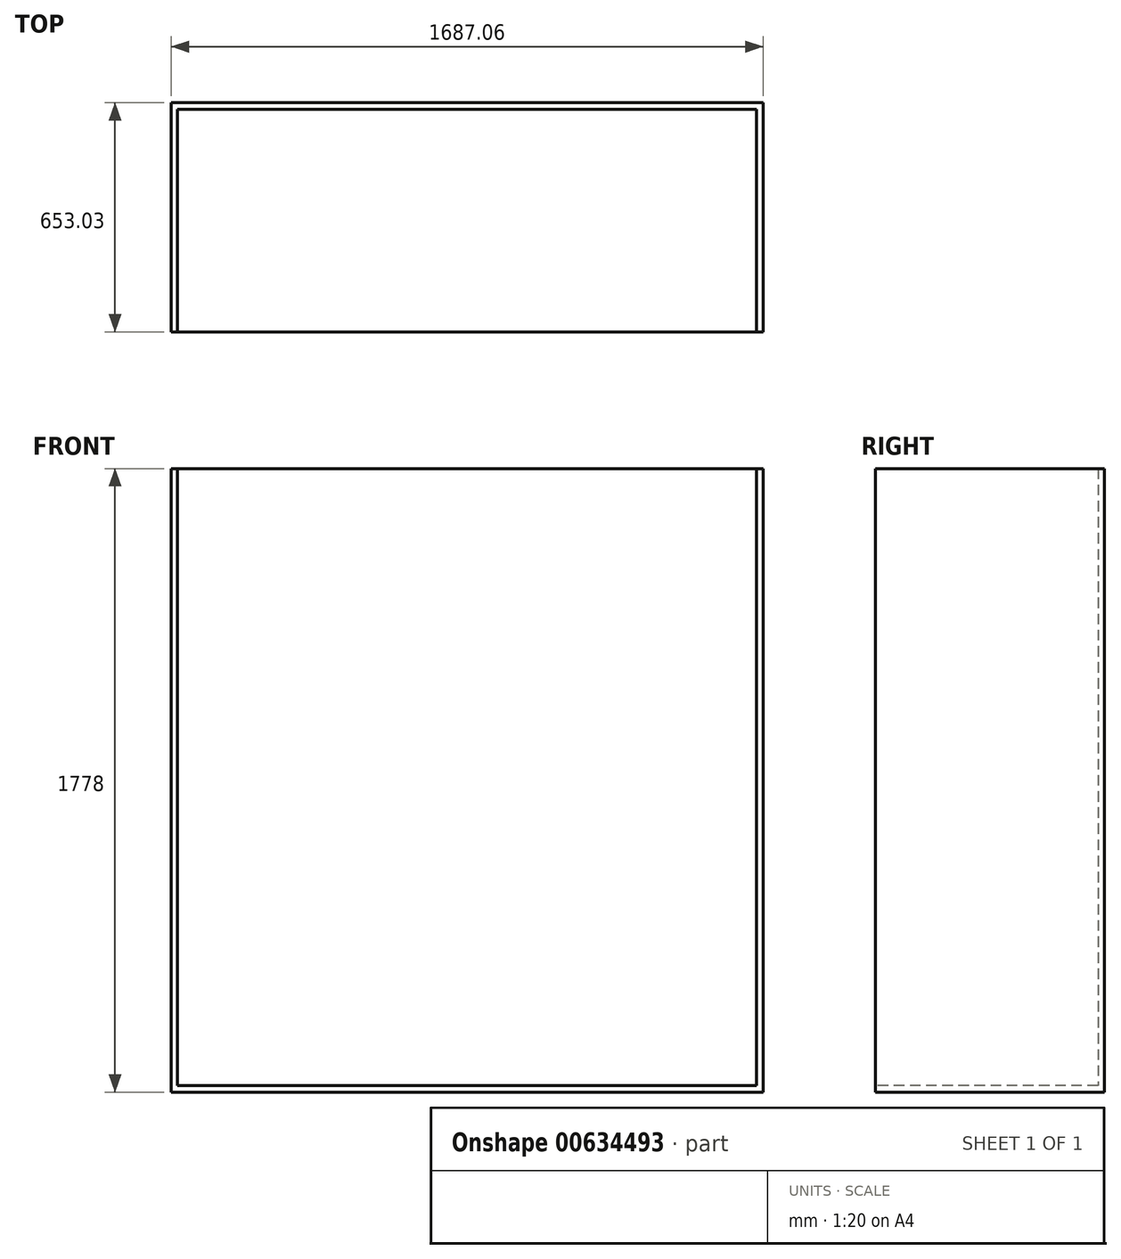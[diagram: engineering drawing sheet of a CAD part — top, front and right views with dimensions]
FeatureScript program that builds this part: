
annotation { "Feature Type Name" : "Feature", "Feature Type Description" : "" }
export const myFeature = defineFeature(function(context is Context, id is Id, definition is map)
    precondition{}
    {
        {
            var Q0;
            Q0=qCreatedBy(makeId("Top.planeOp"),FACE);
            var sketch = newSketch(context, id + "F0", { "sketchPlane" : qUnion([Q0])});
            skLineSegment(sketch, "E0.bottom", {"start": v(-825.5, 317.5) * mm, "end": v(825.5, 317.5) * mm});
            skLineSegment(sketch, "E0.top", {"start": v(-825.5, -317.5) * mm, "end": v(825.5, -317.5) * mm});
            skLineSegment(sketch, "E0.left", {"start": v(-825.5, 317.5) * mm, "end": v(-825.5, -317.5) * mm});
            skLineSegment(sketch, "E0.right", {"start": v(825.5, 317.5) * mm, "end": v(825.5, -317.5) * mm});
            skPoint(sketch, "E0.middle", {"position": v(0, 0) * mm});
            skLineSegment(sketch, "E1.bottom", {"start": v(-825.5, 317.5) * mm, "end": v(-843.53, 317.5) * mm});
            skLineSegment(sketch, "E1.top", {"start": v(-825.5, -317.5) * mm, "end": v(-843.53, -317.5) * mm});
            skLineSegment(sketch, "E1.right", {"start": v(-843.53, 317.5) * mm, "end": v(-843.53, -317.5) * mm});
            skLineSegment(sketch, "E2.bottom", {"start": v(825.5, 317.5) * mm, "end": v(843.53, 317.5) * mm});
            skLineSegment(sketch, "E2.top", {"start": v(825.5, -317.5) * mm, "end": v(843.53, -317.5) * mm});
            skLineSegment(sketch, "E2.right", {"start": v(843.53, 317.5) * mm, "end": v(843.53, -317.5) * mm});
            skLineSegment(sketch, "E3.bottom", {"start": v(-843.53, 317.5) * mm, "end": v(843.53, 317.5) * mm});
            skLineSegment(sketch, "E3.top", {"start": v(-843.53, 335.53) * mm, "end": v(843.53, 335.53) * mm});
            skLineSegment(sketch, "E3.left", {"start": v(-843.53, 317.5) * mm, "end": v(-843.53, 335.53) * mm});
            skLineSegment(sketch, "E3.right", {"start": v(843.53, 317.5) * mm, "end": v(843.53, 335.53) * mm});
            skLineSegment(sketch, "E4.bottom", {"start": v(-177.8, 317.5) * mm, "end": v(-159.77, 317.5) * mm});
            skLineSegment(sketch, "E4.top", {"start": v(-177.8, -317.5) * mm, "end": v(-159.77, -317.5) * mm});
            skLineSegment(sketch, "E4.left", {"start": v(-177.8, 317.5) * mm, "end": v(-177.8, -317.5) * mm});
            skLineSegment(sketch, "E4.right", {"start": v(-159.77, 317.5) * mm, "end": v(-159.77, -317.5) * mm});
            skSolve(sketch);
        }
        {
            var Q0;
            Q0=makeQuery(id+"F0.imprint","IMPRINT",FACE,{"disambiguationData":[TD([[makeQuery(id+"F0.imprint","IMPRINT",EDGE,{"derivedFrom":sQuery(id+"F0.wireOp",EDGE,"E0.top")}),1.0]])]});
            extrude(context, id + "F1", {"entities" : qUnion([Q0]), "depth" : 18.03 * mm, "offsetDistance" : 25.4 * mm});
        }
        {
            var Q0;
            Q0=makeQuery(id+"F0.imprint","IMPRINT",FACE,{"disambiguationData":[TD([[makeQuery(id+"F0.imprint","IMPRINT",EDGE,{"derivedFrom":sQuery(id+"F0.wireOp",EDGE,"E1.top")}),-1.0]])]});
            var Q1;
            Q1=makeQuery(id+"F0.imprint","IMPRINT",FACE,{"disambiguationData":[TD([[makeQuery(id+"F0.imprint","IMPRINT",EDGE,{"derivedFrom":sQuery(id+"F0.wireOp",EDGE,"E2.top")}),1.0]])]});
            var Q2;
            Q2=makeQuery(id+"F0.imprint","IMPRINT",FACE,{"disambiguationData":[TD([[makeQuery(id+"F0.imprint","IMPRINT",EDGE,{"derivedFrom":sQuery(id+"F0.wireOp",EDGE,"E3.top")}),-1.0]])]});
            var Q3;
            Q3=makeQuery(id+"F0.imprint","IMPRINT",FACE,{"disambiguationData":[TD([[makeQuery(id+"F0.imprint","IMPRINT",EDGE,{"derivedFrom":sQuery(id+"F0.wireOp",EDGE,"E4.bottom")}),-1.0]])]});
            extrude(context, id + "F2", {"entities" : qUnion([Q0, Q1, Q2, Q3]), "operationType" : NewBodyOperationType.ADD, "depth" : 1778 * mm, "offsetDistance" : 25.4 * mm});
        }
    });
